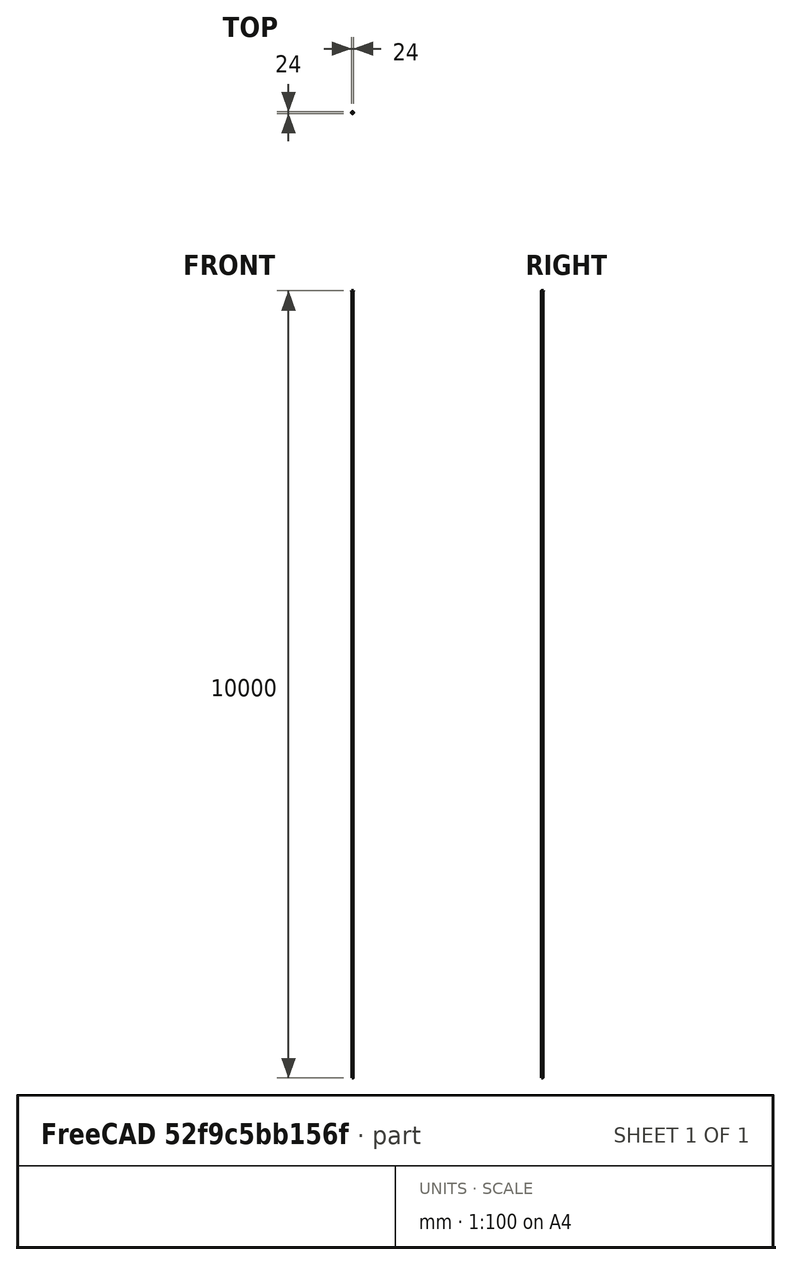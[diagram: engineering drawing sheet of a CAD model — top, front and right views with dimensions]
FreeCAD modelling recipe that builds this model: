
FCSTD DOCUMENT  (FreeCAD 0.16R)
Label: CrankSpacer
License: All rights reserved
LicenseURL: http://en.wikipedia.org/wiki/All_rights_reserved
objects: Sketcher::SketchObject×2, PartDesign::Pad×1, PartDesign::Pocket×1, Mesh::Feature×1
note: 6 computed .brp shape members not serialized (recipe doc carries the construction recipe); baked Part::Feature solids carry a one-line shape summary decoded from their .brp

FEATURE [Sketcher::SketchObject] Sketch
  sketch-geometry (1):
    g0: Circle CenterX=0 CenterY=0 CenterZ=0 NormalX=0 NormalY=0 NormalZ=1 Radius=12
  constraints (2):
    c: Coincident(g0,g-1)
    c: Radius(g0) = 12
FEATURE [PartDesign::Pad] Pad
  Length = 6
  Length2 = 100
  Sketch = -> Sketch
  Type = 0
FEATURE [Sketcher::SketchObject] Sketch001
  Placement = pos=(0,0,6) rot=(0,0,1;0rad)
  Support = -> Pad [Face3]
  sketch-geometry (1):
    g0: Circle CenterX=0 CenterY=0 CenterZ=0 NormalX=0 NormalY=0 NormalZ=1 Radius=7.65
  constraints (2):
    c: Coincident(g0,g-1)
    c: Radius(g0) = 7.65
FEATURE [PartDesign::Pocket] Pocket
  Length = 5
  Sketch = -> Sketch001
  Type = 1
FEATURE [Mesh::Feature] Mesh  label="Pocket (Meshed)"
